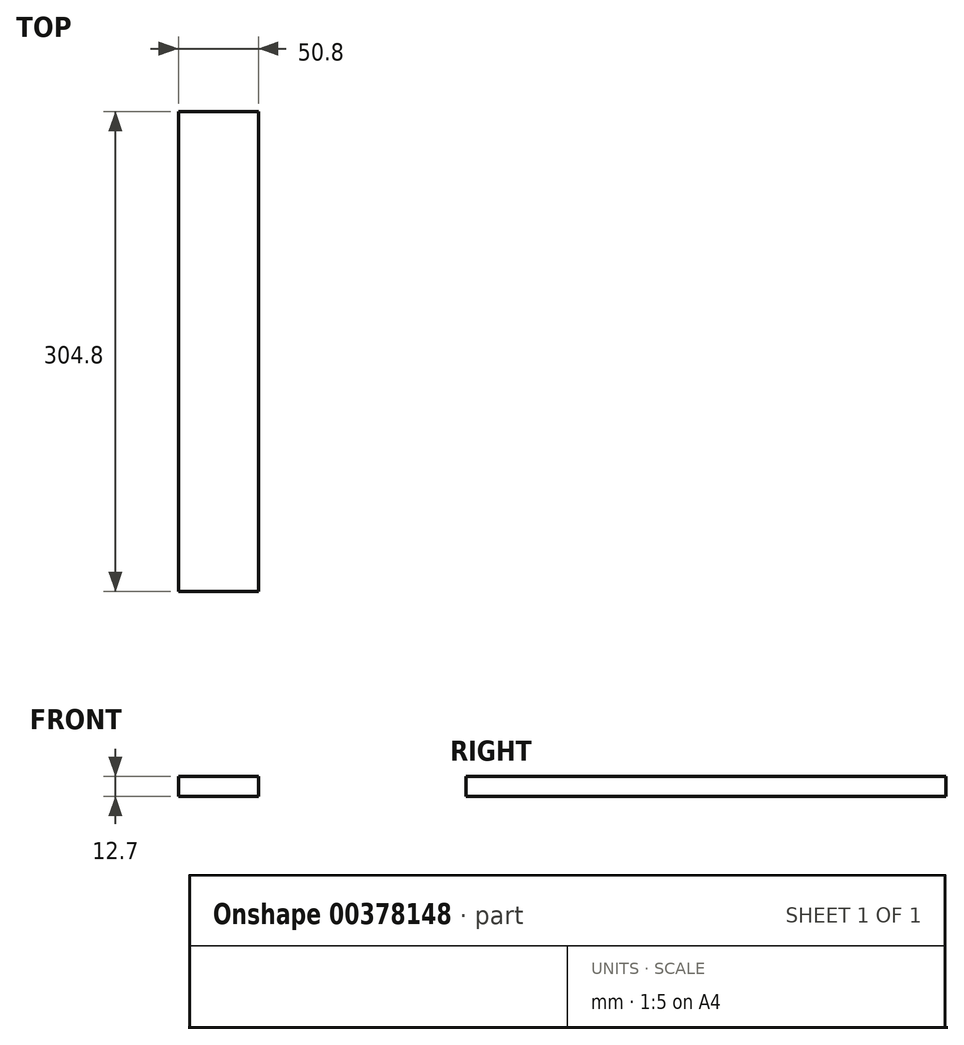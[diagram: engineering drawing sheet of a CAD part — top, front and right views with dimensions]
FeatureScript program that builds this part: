
annotation { "Feature Type Name" : "Feature", "Feature Type Description" : "" }
export const myFeature = defineFeature(function(context is Context, id is Id, definition is map)
    precondition{}
    {
        {
            var Q0;
            Q0=qCreatedBy(makeId("Front.planeOp"),FACE);
            var sketch = newSketch(context, id + "F0", { "sketchPlane" : qUnion([Q0])});
            skLineSegment(sketch, "E0.bottom", {"start": v(25.4, 6.35) * mm, "end": v(-25.4, 6.35) * mm});
            skLineSegment(sketch, "E0.top", {"start": v(25.4, -6.35) * mm, "end": v(-25.4, -6.35) * mm});
            skLineSegment(sketch, "E0.left", {"start": v(25.4, 6.35) * mm, "end": v(25.4, -6.35) * mm});
            skLineSegment(sketch, "E0.right", {"start": v(-25.4, 6.35) * mm, "end": v(-25.4, -6.35) * mm});
            skPoint(sketch, "E0.middle", {"position": v(0, 0) * mm});
            skSolve(sketch);
        }
        {
            var Q0;
            Q0=qSketchRegion(id+"F0",true);
            extrude(context, id + "F1", {"entities" : qUnion([Q0]), "endBound" : BoundingType.SYMMETRIC, "depth" : 304.8 * mm});
        }
    });
